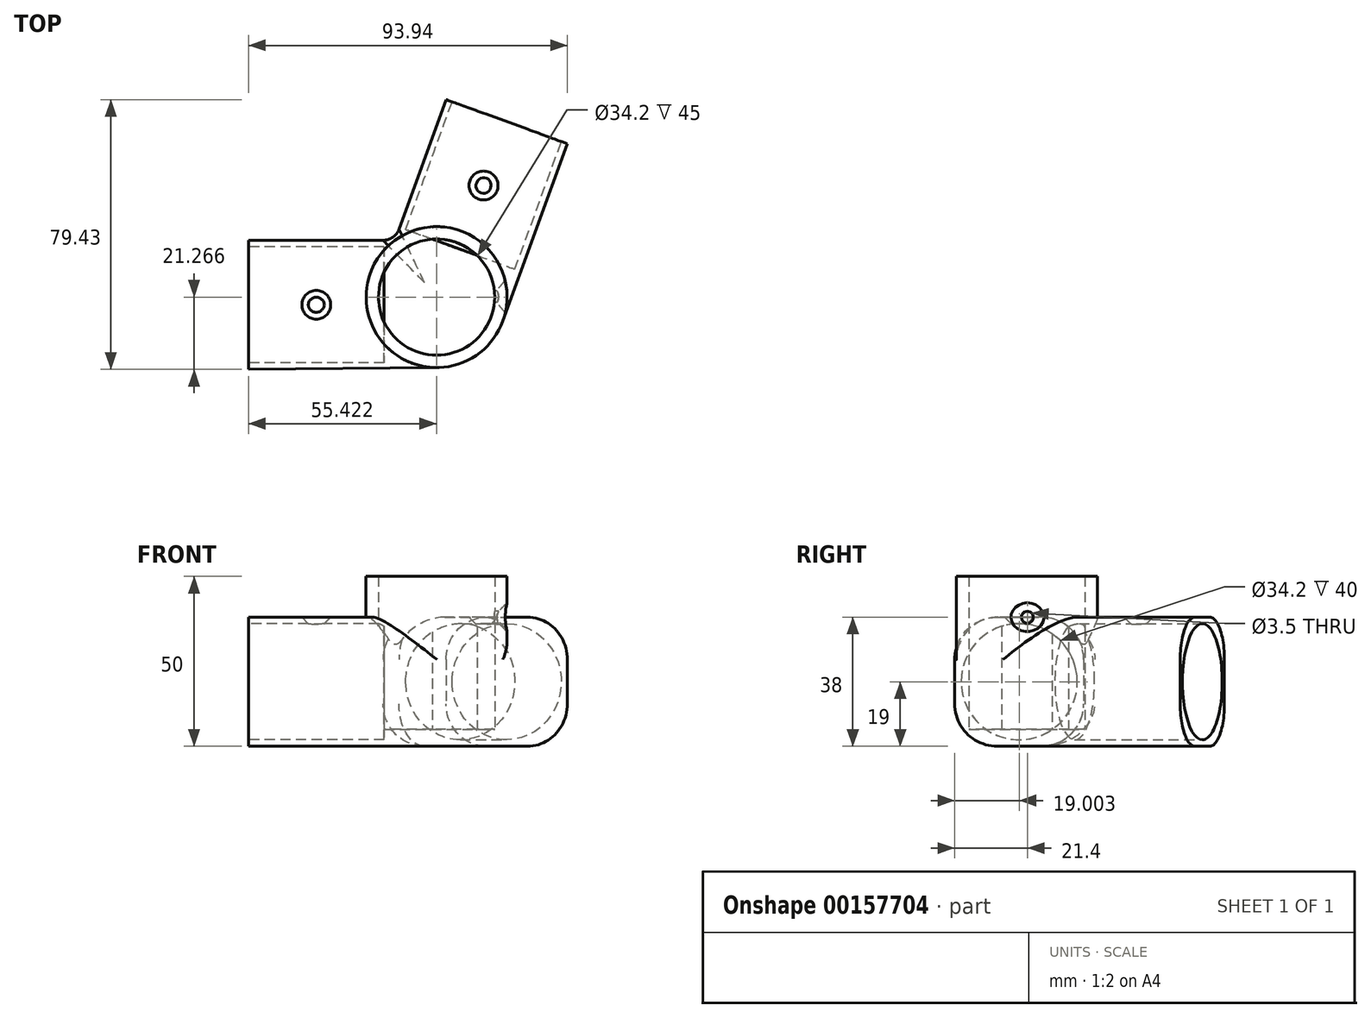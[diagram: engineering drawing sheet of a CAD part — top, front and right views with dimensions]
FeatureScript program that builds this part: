
annotation { "Feature Type Name" : "Feature", "Feature Type Description" : "" }
export const myFeature = defineFeature(function(context is Context, id is Id, definition is map)
    precondition{}
    {
        {
            var Q0;
            Q0=qCreatedBy(makeId("Top.planeOp"),FACE);
            var sketch = newSketch(context, id + "F0", { "sketchPlane" : qUnion([Q0])});
            skLineSegment(sketch, "E0.bottom", {"start": v(0, 0) * mm, "end": v(-70, -0.65) * mm});
            skLineSegment(sketch, "E0.right", {"start": v(-70, -0.65) * mm, "end": v(-70, 37.35) * mm});
            skLineSegment(sketch, "E1", {"start": v(0, 0) * mm, "end": v(23.94, 65.78) * mm});
            skLineSegment(sketch, "E2", {"start": v(-26.84, 37.35) * mm, "end": v(-11.77, 78.78) * mm});
            skLineSegment(sketch, "E3", {"start": v(-11.77, 78.78) * mm, "end": v(23.94, 65.78) * mm});
            skCircle(sketch, "E4", {"center": v(-14.58, 20.62) * mm, "radius": 20.75 * mm});
            skLineSegment(sketch, "E5", {"start": v(-14.82, 20.75) * mm, "end": v(0, 0) * mm, "construction": true});
            skCircle(sketch, "E6", {"center": v(-14.58, 20.62) * mm, "radius": 17.1 * mm});
            skLineSegment(sketch, "E7.trimOffspring", {"start": v(-26.84, 37.35) * mm, "end": v(-70, 37.35) * mm});
            skPoint(sketch, "E8", {"position": v(6.09, 72.28) * mm});
            skPoint(sketch, "E9", {"position": v(-70, 18.35) * mm});
            skLineSegment(sketch, "E10", {"start": v(6.09, 72.28) * mm, "end": v(-0.75, 53.48) * mm, "construction": true});
            skLineSegment(sketch, "E11", {"start": v(-70, 18.35) * mm, "end": v(-50, 18.35) * mm, "construction": true});
            skCircle(sketch, "E12", {"center": v(-50, 18.35) * mm, "radius": 1.75 * mm});
            skCircle(sketch, "E13", {"center": v(-0.75, 53.48) * mm, "radius": 1.75 * mm});
            skSolve(sketch);
        }
        {
            var Q0;
            {var subQ4=sQuery(id+"F0.wireOp",EDGE,"E0.right");Q0=makeQuery(id+"F0.imprint","IMPRINT",FACE,{"disambiguationData":[TD([[makeQuery(id+"F0.imprint","IMPRINT",EDGE,{"derivedFrom":subQ4}),-1.0]])]});}
            var Q1;
            Q1=makeQuery(id+"F0.imprint","IMPRINT",FACE,{"disambiguationData":[TD([[makeQuery(id+"F0.imprint","IMPRINT",EDGE,{"derivedFrom":sQuery(id+"F0.wireOp",EDGE,"E12")}),1.0]])]});
            var Q2;
            {var subQ1=sQuery(id+"F0.wireOp",EDGE,"E2");Q2=makeQuery(id+"F0.imprint","IMPRINT",FACE,{"disambiguationData":[TD([[makeQuery(id+"F0.imprint","IMPRINT",EDGE,{"derivedFrom":subQ1}),-1.0]])]});}
            var Q3;
            Q3=makeQuery(id+"F0.imprint","IMPRINT",FACE,{"disambiguationData":[TD([[makeQuery(id+"F0.imprint","IMPRINT",EDGE,{"derivedFrom":sQuery(id+"F0.wireOp",EDGE,"E13")}),1.0]])]});
            extrude(context, id + "F1", {"entities" : qUnion([Q0, Q1, Q2, Q3]), "depth" : 38 * mm});
        }
        {
            var Q0;
            Q0=makeQuery(id+"F0.imprint","IMPRINT",FACE,{"disambiguationData":[TD([[makeQuery(id+"F0.imprint","IMPRINT",EDGE,{"derivedFrom":sQuery(id+"F0.wireOp",EDGE,"E6")}),-1.0]])]});
            extrude(context, id + "F2", {"entities" : qUnion([Q0]), "operationType" : NewBodyOperationType.ADD, "depth" : 50 * mm});
        }
        {
            var Q0;
            Q0=makeQuery(id+"F0.imprint","IMPRINT",FACE,{"disambiguationData":[TD([[makeQuery(id+"F0.imprint","IMPRINT",EDGE,{"derivedFrom":sQuery(id+"F0.wireOp",EDGE,"E6")}),1.0]])]});
            extrude(context, id + "F3", {"entities" : qUnion([Q0]), "operationType" : NewBodyOperationType.ADD, "depth" : 5 * mm});
        }
        {
            var Q0;
            {var subQ0=sQuery(id+"F0.wireOp",EDGE,"E0.bottom");Q0=makeQuery(id+"F2.boolean.opBoolean","MERGE",EDGE,{"derivedFrom":[makeQuery(id+"F1.opExtrude","CAP_EDGE",EDGE,{"disambiguationData":[OSD([subQ0])],"isStart":true}),makeQuery(id+"F2.opExtrude","CAP_EDGE",EDGE,{"disambiguationData":[OSD([subQ0])],"isStart":true})]});}
            var Q1;
            Q1=makeQuery(id+"F1.opExtrude","CAP_EDGE",EDGE,{"disambiguationData":[OSD([sQuery(id+"F0.wireOp",EDGE,"E0.bottom")])],"isStart":false});
            var Q2;
            Q2=makeQuery(id+"F1.opExtrude","CAP_EDGE",EDGE,{"disambiguationData":[OSD([sQuery(id+"F0.wireOp",EDGE,"E1")])],"isStart":false});
            var Q3;
            {var subQ0=sQuery(id+"F0.wireOp",EDGE,"E1");Q3=makeQuery(id+"F2.boolean.opBoolean","MERGE",EDGE,{"derivedFrom":[makeQuery(id+"F1.opExtrude","CAP_EDGE",EDGE,{"disambiguationData":[OSD([subQ0])],"isStart":true}),makeQuery(id+"F2.opExtrude","CAP_EDGE",EDGE,{"disambiguationData":[OSD([subQ0])],"isStart":true})]});}
            fillet(context, id + "F4", {"entities" : qUnion([Q0, Q1, Q2, Q3]), "radius" : 12.5 * mm, "allowEdgeOverflow" : false});
        }
        {
            var Q0;
            Q0=makeQuery(id+"F1.opExtrude","CAP_EDGE",EDGE,{"disambiguationData":[OSD([sQuery(id+"F0.wireOp",EDGE,"E2")])],"isStart":false});
            fillet(context, id + "F5", {"entities" : qUnion([Q0]), "radius" : 12.5 * mm, "tangentPropagation" : true, "allowEdgeOverflow" : false});
        }
        {
            var Q0;
            Q0=makeQuery(id+"F1.opExtrude","CAP_EDGE",EDGE,{"disambiguationData":[OSD([sQuery(id+"F0.wireOp",EDGE,"E7.trimOffspring")])],"isStart":false});
            fillet(context, id + "F6", {"entities" : qUnion([Q0]), "radius" : 12.5 * mm, "tangentPropagation" : true, "allowEdgeOverflow" : false});
        }
        {
            var Q0;
            Q0=makeQuery(id+"F1.opExtrude","CAP_EDGE",EDGE,{"disambiguationData":[OSD([sQuery(id+"F0.wireOp",EDGE,"E2")])],"isStart":true});
            fillet(context, id + "F7", {"entities" : qUnion([Q0]), "radius" : 12.5 * mm, "allowEdgeOverflow" : false});
        }
        {
            var Q0;
            Q0=makeQuery(id+"F1.opExtrude","CAP_EDGE",EDGE,{"disambiguationData":[OSD([sQuery(id+"F0.wireOp",EDGE,"E7.trimOffspring")])],"isStart":true});
            var Q1;
            Q1=makeQuery(id+"F1.opExtrude","CAP_EDGE",EDGE,{"disambiguationData":[OSD([sQuery(id+"F0.wireOp",EDGE,"E0.bottom")])],"isStart":true});
            var Q2;
            Q2=makeQuery(id+"F1.opExtrude","CAP_EDGE",EDGE,{"disambiguationData":[OSD([sQuery(id+"F0.wireOp",EDGE,"E1")])],"isStart":true});
            fillet(context, id + "F8", {"entities" : qUnion([Q0, Q1, Q2]), "radius" : 12.5 * mm, "allowEdgeOverflow" : false});
        }
        {
            var Q0;
            Q0=makeQuery(id+"F1.opExtrude","SWEPT_FACE",FACE,{"disambiguationData":[OSD([sQuery(id+"F0.wireOp",EDGE,"E0.right")])]});
            var sketch = newSketch(context, id + "F9", { "sketchPlane" : qUnion([Q0])});
            skCircle(sketch, "E14", {"center": v(-18.35, 19) * mm, "radius": 17.1 * mm});
            skLineSegment(sketch, "E15", {"start": v(-37.35, 19) * mm, "end": v(0.65, 19) * mm, "construction": true});
            skSolve(sketch);
        }
        {
            var Q0;
            Q0=makeQuery(id+"F9.imprint","IMPRINT",FACE,{"disambiguationData":[TD([[makeQuery(id+"F9.imprint","IMPRINT",EDGE,{"derivedFrom":sQuery(id+"F9.wireOp",EDGE,"E14")}),1.0]])]});
            extrude(context, id + "F10", {"entities" : qUnion([Q0]), "operationType" : NewBodyOperationType.REMOVE, "oppositeDirection" : true, "depth" : 40 * mm});
        }
        {
            var Q0;
            Q0=makeQuery(id+"F1.opExtrude","SWEPT_FACE",FACE,{"disambiguationData":[OSD([sQuery(id+"F0.wireOp",EDGE,"E3")])]});
            var sketch = newSketch(context, id + "F11", { "sketchPlane" : qUnion([Q0])});
            skCircle(sketch, "E16", {"center": v(19, 19) * mm, "radius": 17.1 * mm});
            skLineSegment(sketch, "E17", {"start": v(19, 38) * mm, "end": v(19, 0) * mm, "construction": true});
            skSolve(sketch);
        }
        {
            var Q0;
            Q0=makeQuery(id+"F11.imprint","IMPRINT",FACE,{"disambiguationData":[TD([[makeQuery(id+"F11.imprint","IMPRINT",EDGE,{"derivedFrom":sQuery(id+"F11.wireOp",EDGE,"E16")}),1.0]])]});
            extrude(context, id + "F12", {"entities" : qUnion([Q0]), "operationType" : NewBodyOperationType.REMOVE, "oppositeDirection" : true, "depth" : 40 * mm});
        }
        {
            var Q0;
            Q0=qCreatedBy(makeId("Right.planeOp"),FACE);
            var sketch = newSketch(context, id + "F13", { "sketchPlane" : qUnion([Q0])});
            skCircle(sketch, "E18", {"center": v(20.75, 38) * mm, "radius": 1.75 * mm});
            skLineSegment(sketch, "E19", {"start": v(16.54, 38) * mm, "end": v(24.96, 38) * mm, "construction": true});
            skSolve(sketch);
        }
        {
            var Q0;
            Q0=makeQuery(id+"F0.imprint","IMPRINT",FACE,{"disambiguationData":[TD([[makeQuery(id+"F0.imprint","IMPRINT",EDGE,{"derivedFrom":sQuery(id+"F0.wireOp",EDGE,"E12")}),1.0]])]});
            var Q1;
            Q1=makeQuery(id+"F0.imprint","IMPRINT",FACE,{"disambiguationData":[TD([[makeQuery(id+"F0.imprint","IMPRINT",EDGE,{"derivedFrom":sQuery(id+"F0.wireOp",EDGE,"E13")}),1.0]])]});
            extrude(context, id + "F14", {"entities" : qUnion([Q0, Q1]), "operationType" : NewBodyOperationType.REMOVE, "depth" : 45 * mm, "hasSecondDirection" : true, "secondDirectionOppositeDirection" : false, "secondDirectionDepth" : 35 * mm});
        }
        {
            var Q0;
            Q0=makeQuery(id+"F13.imprint","IMPRINT",FACE,{"disambiguationData":[TD([[makeQuery(id+"F13.imprint","IMPRINT",EDGE,{"derivedFrom":sQuery(id+"F13.wireOp",EDGE,"E18")}),1.0]])]});
            extrude(context, id + "F15", {"entities" : qUnion([Q0]), "operationType" : NewBodyOperationType.REMOVE, "depth" : 10 * mm});
        }
        {
            var Q0;
            Q0=makeQuery(id+"F14.boolean.opBoolean","INTERSECT",EDGE,{"derivedFrom":[makeQuery(id+"F5.opFillet","SPLIT",FACE,{"disambiguationData":[OD(1.0)],"derivedFrom":makeQuery(id+"F1.opExtrude","CAP_FACE",FACE,{"disambiguationData":[OSD([sQuery(id+"F0.wireOp",EDGE,"E0.bottom"),sQuery(id+"F0.wireOp",EDGE,"E0.right"),sQuery(id+"F0.wireOp",EDGE,"E1"),sQuery(id+"F0.wireOp",EDGE,"E2"),sQuery(id+"F0.wireOp",EDGE,"E3"),sQuery(id+"F0.wireOp",EDGE,"E4"),sQuery(id+"F0.wireOp",EDGE,"E7.trimOffspring")])],"isStart":false})}),makeQuery(id+"F14.opExtrude","SWEPT_FACE",FACE,{"disambiguationData":[OSD([sQuery(id+"F0.wireOp",EDGE,"E13")])]})]});
            var Q1;
            Q1=makeQuery(id+"F14.boolean.opBoolean","INTERSECT",EDGE,{"derivedFrom":[makeQuery(id+"F5.opFillet","SPLIT",FACE,{"disambiguationData":[OD(0.0)],"derivedFrom":makeQuery(id+"F1.opExtrude","CAP_FACE",FACE,{"disambiguationData":[OSD([sQuery(id+"F0.wireOp",EDGE,"E0.bottom"),sQuery(id+"F0.wireOp",EDGE,"E0.right"),sQuery(id+"F0.wireOp",EDGE,"E1"),sQuery(id+"F0.wireOp",EDGE,"E2"),sQuery(id+"F0.wireOp",EDGE,"E3"),sQuery(id+"F0.wireOp",EDGE,"E4"),sQuery(id+"F0.wireOp",EDGE,"E7.trimOffspring")])],"isStart":false})}),makeQuery(id+"F14.opExtrude","SWEPT_FACE",FACE,{"disambiguationData":[OSD([sQuery(id+"F0.wireOp",EDGE,"E12")])]})]});
            var Q2;
            {var subQ0=sQuery(id+"F0.wireOp",EDGE,"E4");Q2=makeQuery(id+"F15.boolean.opBoolean","INTERSECT",EDGE,{"derivedFrom":[makeQuery(id+"F2.opExtrude","SWEPT_FACE",FACE,{"disambiguationData":[OSD([subQ0]),TDD([makeQuery(id+"F0.imprint","IMPRINT",EDGE,{"disambiguationData":[TD([[makeQuery(id+"F0.imprint","INTERSECT",VERTEX,{"disambiguationData":[OD(0.0)],"derivedFrom":[sQuery(id+"F0.wireOp",EDGE,"E0.bottom"),subQ0]}),-1.0]])],"derivedFrom":subQ0})])]}),makeQuery(id+"F15.opExtrude","SWEPT_FACE",FACE,{"disambiguationData":[OSD([sQuery(id+"F13.wireOp",EDGE,"E18")])]})]});}
            var Q3;
            Q3=makeQuery(id+"F15.boolean.opBoolean","COPY",EDGE,{"disambiguationData":[OD(0.0)],"derivedFrom":makeQuery(id+"F15.opExtrude","CAP_EDGE",EDGE,{"disambiguationData":[OSD([sQuery(id+"F13.wireOp",EDGE,"E18")])],"isStart":true})});
            var Q4;
            {var subQ0=sQuery(id+"F0.wireOp",EDGE,"E4");Q4=makeQuery(id+"F15.boolean.opBoolean","INTERSECT",EDGE,{"derivedFrom":[makeQuery(id+"F2.opExtrude","SWEPT_FACE",FACE,{"disambiguationData":[OSD([subQ0]),TDD([makeQuery(id+"F0.imprint","IMPRINT",EDGE,{"disambiguationData":[TD([[makeQuery(id+"F0.imprint","INTERSECT",VERTEX,{"disambiguationData":[OD(1.0)],"derivedFrom":[sQuery(id+"F0.wireOp",EDGE,"E0.bottom"),subQ0]}),1.0]])],"derivedFrom":subQ0})])]}),makeQuery(id+"F15.opExtrude","SWEPT_FACE",FACE,{"disambiguationData":[OSD([sQuery(id+"F13.wireOp",EDGE,"E18")])]})]});}
            var Q5;
            Q5=makeQuery(id+"F15.boolean.opBoolean","COPY",EDGE,{"disambiguationData":[OD(1.0)],"derivedFrom":makeQuery(id+"F15.opExtrude","CAP_EDGE",EDGE,{"disambiguationData":[OSD([sQuery(id+"F13.wireOp",EDGE,"E18")])],"isStart":true})});
            chamfer(context, id + "F16", {"entities" : qUnion([Q0, Q1, Q2, Q3, Q4, Q5]), "width" : 2.5 * mm, "tangentPropagation" : true});
        }
        {
            var Q0;
            {var subQ0=sQuery(id+"F0.wireOp",EDGE,"E0.bottom");var subQ1=sQuery(id+"F0.wireOp",EDGE,"E4");var subQ2=sQuery(id+"F0.wireOp",EDGE,"E7.trimOffspring");var subQ3=sQuery(id+"F0.wireOp",EDGE,"E2");var subQ4=sQuery(id+"F0.wireOp",EDGE,"E1");Q0=makeQuery(id+"F2.boolean.opBoolean","MERGE",EDGE,{"derivedFrom":[makeQuery(id+"F1.opExtrude","SWEPT_EDGE",EDGE,{"disambiguationData":[OSD([subQ3,subQ1,subQ2]),ownerDisambiguation([makeQuery(id+"F0.imprint","IMPRINT",EDGE,{"disambiguationData":[TD([[makeQuery(id+"F0.imprint","INTERSECT",VERTEX,{"derivedFrom":[subQ4,sQuery(id+"F0.wireOp",EDGE,"E3")]}),1.0]])],"derivedFrom":subQ4})])]}),makeQuery(id+"F1.opExtrude","SWEPT_EDGE",EDGE,{"disambiguationData":[OSD([subQ3,subQ1,subQ2]),ownerDisambiguation([makeQuery(id+"F0.imprint","IMPRINT",EDGE,{"disambiguationData":[TD([[makeQuery(id+"F0.imprint","INTERSECT",VERTEX,{"derivedFrom":[subQ0,sQuery(id+"F0.wireOp",EDGE,"E0.right")]}),1.0]])],"derivedFrom":subQ0})])]})]});}
            fillet(context, id + "F17", {"entities" : qUnion([Q0]), "radius" : 5 * mm, "tangentPropagation" : true, "allowEdgeOverflow" : false});
        }
    });
